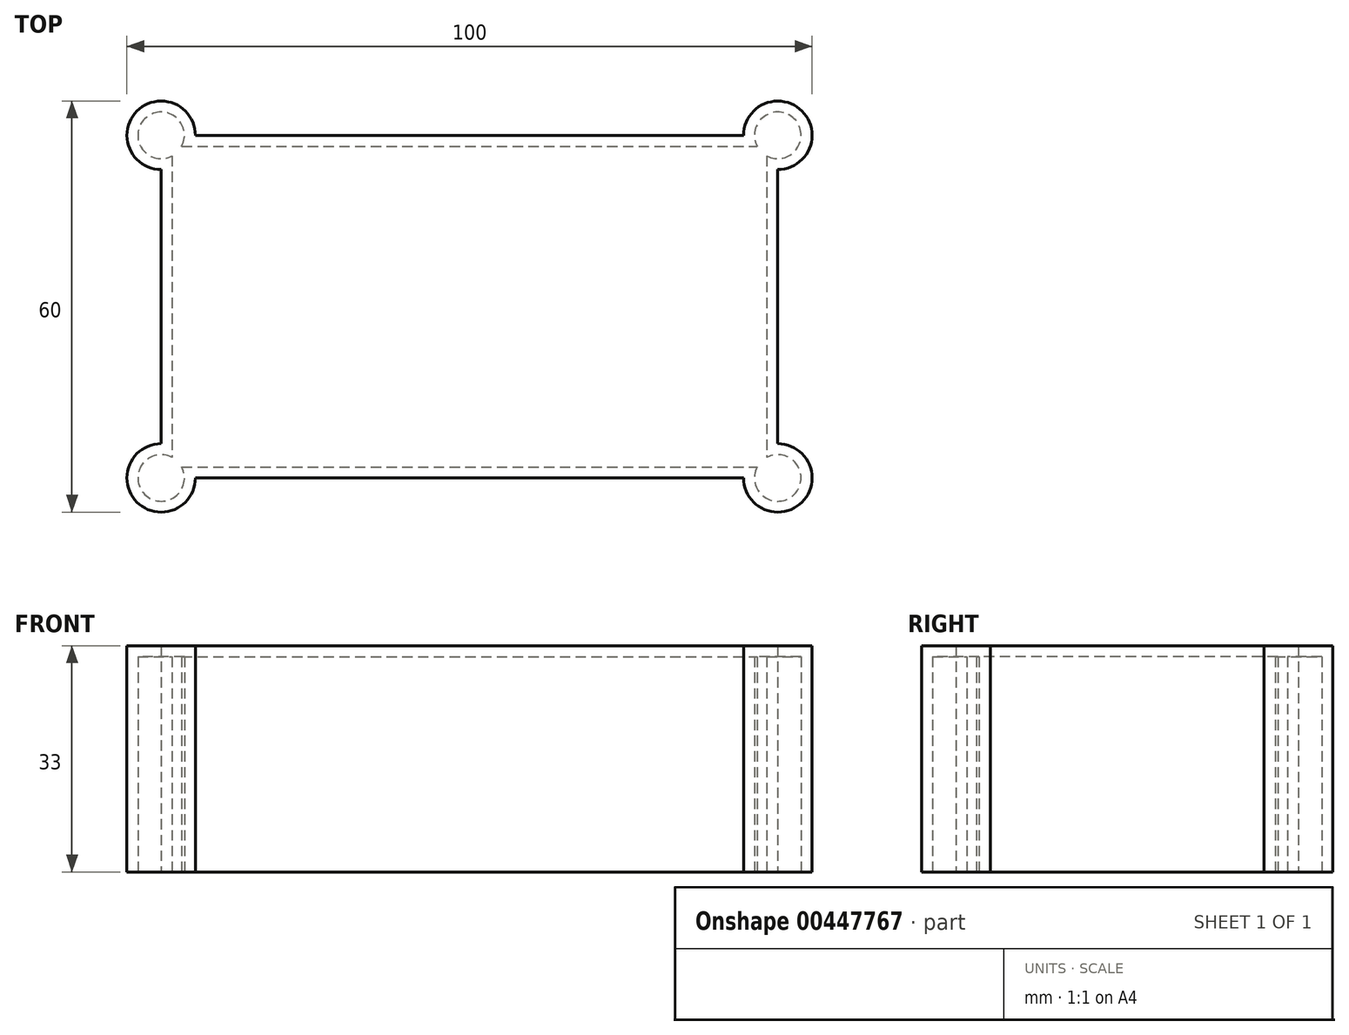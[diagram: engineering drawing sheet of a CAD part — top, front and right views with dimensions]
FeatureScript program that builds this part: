
annotation { "Feature Type Name" : "Feature", "Feature Type Description" : "" }
export const myFeature = defineFeature(function(context is Context, id is Id, definition is map)
    precondition{}
    {
        {
            var Q0;
            Q0=qCreatedBy(makeId("Top.planeOp"),FACE);
            var sketch = newSketch(context, id + "F0", { "sketchPlane" : qUnion([Q0])});
            skLineSegment(sketch, "E0.bottom", {"start": v(-40, 25) * mm, "end": v(40, 25) * mm});
            skLineSegment(sketch, "E0.top", {"start": v(-40, -25) * mm, "end": v(40, -25) * mm});
            skLineSegment(sketch, "E0.left", {"start": v(-45, 20) * mm, "end": v(-45, -20) * mm});
            skLineSegment(sketch, "E0.right", {"start": v(45, 20) * mm, "end": v(45, -20) * mm});
            skPoint(sketch, "E0.middle", {"position": v(0, 0) * mm});
            skArc(sketch, "E1", {"start": v(-40, 25) * mm, "mid": v(-48.54, 28.54) * mm, "end": v(-45, 20) * mm});
            skArc(sketch, "E2", {"start": v(45, 20) * mm, "mid": v(48.54, 28.54) * mm, "end": v(40, 25) * mm});
            skArc(sketch, "E3", {"start": v(40, -25) * mm, "mid": v(48.54, -28.54) * mm, "end": v(45, -20) * mm});
            skArc(sketch, "E4", {"start": v(-45, -20) * mm, "mid": v(-48.54, -28.54) * mm, "end": v(-40, -25) * mm});
            skSolve(sketch);
        }
        {
            var Q0;
            Q0=makeQuery(id+"F0.imprint","IMPRINT",FACE,{"disambiguationData":[TD([[makeQuery(id+"F0.imprint","IMPRINT",EDGE,{"derivedFrom":sQuery(id+"F0.wireOp",EDGE,"E0.bottom")}),-1.0]])]});
            extrude(context, id + "F1", {"entities" : qUnion([Q0]), "depth" : 33 * mm});
        }
        {
            var Q0;
            Q0=makeQuery(id+"F1.opExtrude","CAP_FACE",FACE,{"disambiguationData":[OSD([sQuery(id+"F0.wireOp",EDGE,"E0.bottom"),sQuery(id+"F0.wireOp",EDGE,"E0.top"),sQuery(id+"F0.wireOp",EDGE,"E0.left"),sQuery(id+"F0.wireOp",EDGE,"E0.right"),sQuery(id+"F0.wireOp",EDGE,"E1"),sQuery(id+"F0.wireOp",EDGE,"E2"),sQuery(id+"F0.wireOp",EDGE,"E3"),sQuery(id+"F0.wireOp",EDGE,"E4")])],"isStart":true});
            shell(context, id + "F2", {"entities" : qUnion([Q0]), "thickness" : 1.6 * mm});
        }
    });
